# Revit family: EVID-S5.2X
name_source: partatom
category: Communication Devices
revit_build: Autodesk Revit 2017 (Build: 20160225_1515(x64)
units: mm (PartAtom-declared; Revit-internal decimal feet)

## family parameters
Always vertical = Yes
Cut with Voids When Loaded = No
Maintain Annotation Orientation = Yes
OmniClass Number = 23.85.10.11.11.21
OmniClass Title = Speakers
Part Type = Normal
Room Calculation Point = No
Round Connector Dimension = Use Diameter
Shared = No
Work Plane-Based = Yes

## types (2) — shared parameters
ArchitectsAndEngineersSpecs = https://www.electrovoice.com
CTN = EVIDS5.2XB
Default Elevation = 1219.2 mm  [stored 4 ft]
Depth = 169 mm  [stored 0.554462 ft]
Description = Carefully engineered for the toughest weather conditions (IP65). Long throw 5.25" (133mm) woofer housed in a UL 94-5VB fire rated ABS plastic for extended LF performance down to 55Hz. 90 W power handling provides for 108 dB maximum SPL (114 dB Peak). 60 W transformer with 8 Ohm pass-through.
Disclaimer = http://resource.boschsecurity.com
FrontHeight = 255 mm  [stored 0.836614 ft]
HorizontalErrorText = Maximum 45° allowed per side.
IfcExportAs = IfcBuildingElementProxy
IfcExportType = IfcBuildingElementProxyType
InstallationManual = https://www.electrovoice.com
Length = 180.1 mm  [stored 0.590879 ft]
Manufacturer = Electro Voice
ManufacturerURL = https://www.electrovoice.com
MaterialRALColour = RAL9004
OKText = OK
PlanningTools = https://www.electrovoice.com
ProductInformation = https://www.electrovoice.com
Uniclass2015Code = Pr_60_75_08_02
Version = 1

## per-type parameters (varying)
| type | GrillMaterial | LoudspeakerMaterial | ModelNumber |
| EVIDS5.2XB_Speaker_5”_Cabinet_70/100V_IP65_Black | 16GA Powder-coatedGalvanneal - B | 13-plyWeather-resistantBirchEVCoat -RAL9004 | F.01U.332.738 |
| EVIDS5.2XW_Speaker_5”_Cabinet_70/100V_IP65_White | 16GA Powder-coatedGalvanneal - W | 13-plyWeather-resistantBirchEVCoat -RAL9003 | F.01U.332.739 |

note: [stored X ft] marks values corroborated as IEEE doubles in the binary element streams (Revit-internal decimal feet)

## geometry (parser evidence)
native form markers: Sweep x9
no freeform markers — native parametric forms only
